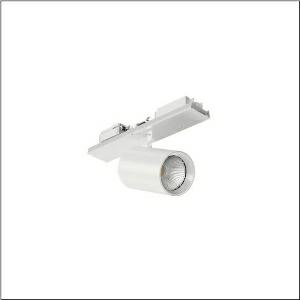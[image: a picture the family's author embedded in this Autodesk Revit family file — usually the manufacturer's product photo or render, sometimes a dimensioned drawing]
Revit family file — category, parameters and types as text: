
# Revit family: licross_r__spot_31_51sl14da43b_e1eb
name_source: partatom
category: Lighting Fixtures
units: mm (PartAtom-declared; Revit-internal decimal feet)

## family parameters
Cut with Voids When Loaded = No
Host = Face
Light Source = No
Part Type = Normal
Room Calculation Point = No
Round Connector Dimension = Use Diameter
Shared = No

## types (1)
- --- (1 x LED, 3720 lm, 28.5 W, 4000K)
    Apparent Load = 29 VA
    CIE Flux Codes = 93 97 100 100 100
    Color Rendering = 90
    Color Temperature = 4000K
    Default Elevation = 1800 mm
    Description = Licross® Spot 31, directional spotlight, light control with lens, of plastic, LED rated luminous flux: 3.720lm, light colour: 940, with plug, 5-pole, mains connection: 220..240V, AC, 50/60Hz, of aluminium, traffic white (RAL 9016), length: 300mm, diameter: 90mm, protection rating (complete): IP20, insulation class (complete): insulation class I (protective earthing), certification: CE, packaging unit: 1 piece
    Height = 175 mm
    Lamp = 1 x LED
    Lamp Light Flux = 3720 lm
    Lamp Power = 28.5 W
    Lamp count = 1
    Length = 90 mm
    Luminous efficacy = 131 lm/W
    Manufacturer = Siteco
    ModVariant = No
    Model = 51SL14DA43B
    Mounting Place = Ceiling
    Mounting Type = Pendant
    Number of Poles = 1
    OnlyDefault = Yes
    Power Factor = 1
    Product Name = Licross® Spot 31
    Product group = directional spotlight
    ProductGroupID = 905
    Protection Class = Protection class I
    Protection Degree = IP 20
    RLX_Detail_Level = 1
    RLX_Emergency_Light_Flux = 0 lm
    RLX_Emergency_Type = 0
    RLX_Emergency_Type_DB = No
    RlxData = <blob elided: 14809 chars, md5=e163b21e>
    Socket = socket
    Standby Power = 0 W
    System Light Flux = 3720 lm
    System Power = 29 W
    Type Comments = factory setting: luminous flux: 100 % | (ON | ON | ON) | 700 mA
    Type Image = l_1245720.jpg
    URL = http://relux.com
    VarID = @adj_153327
    Voltage = 0 V
    Weight = 0.00 kg
    Width = 0 mm  [stored 0 ft]

note: [stored X ft] marks values corroborated as IEEE doubles in the binary element streams (Revit-internal decimal feet)

## geometry (parser evidence)
native form markers: Sweep x12
no freeform markers — native parametric forms only
